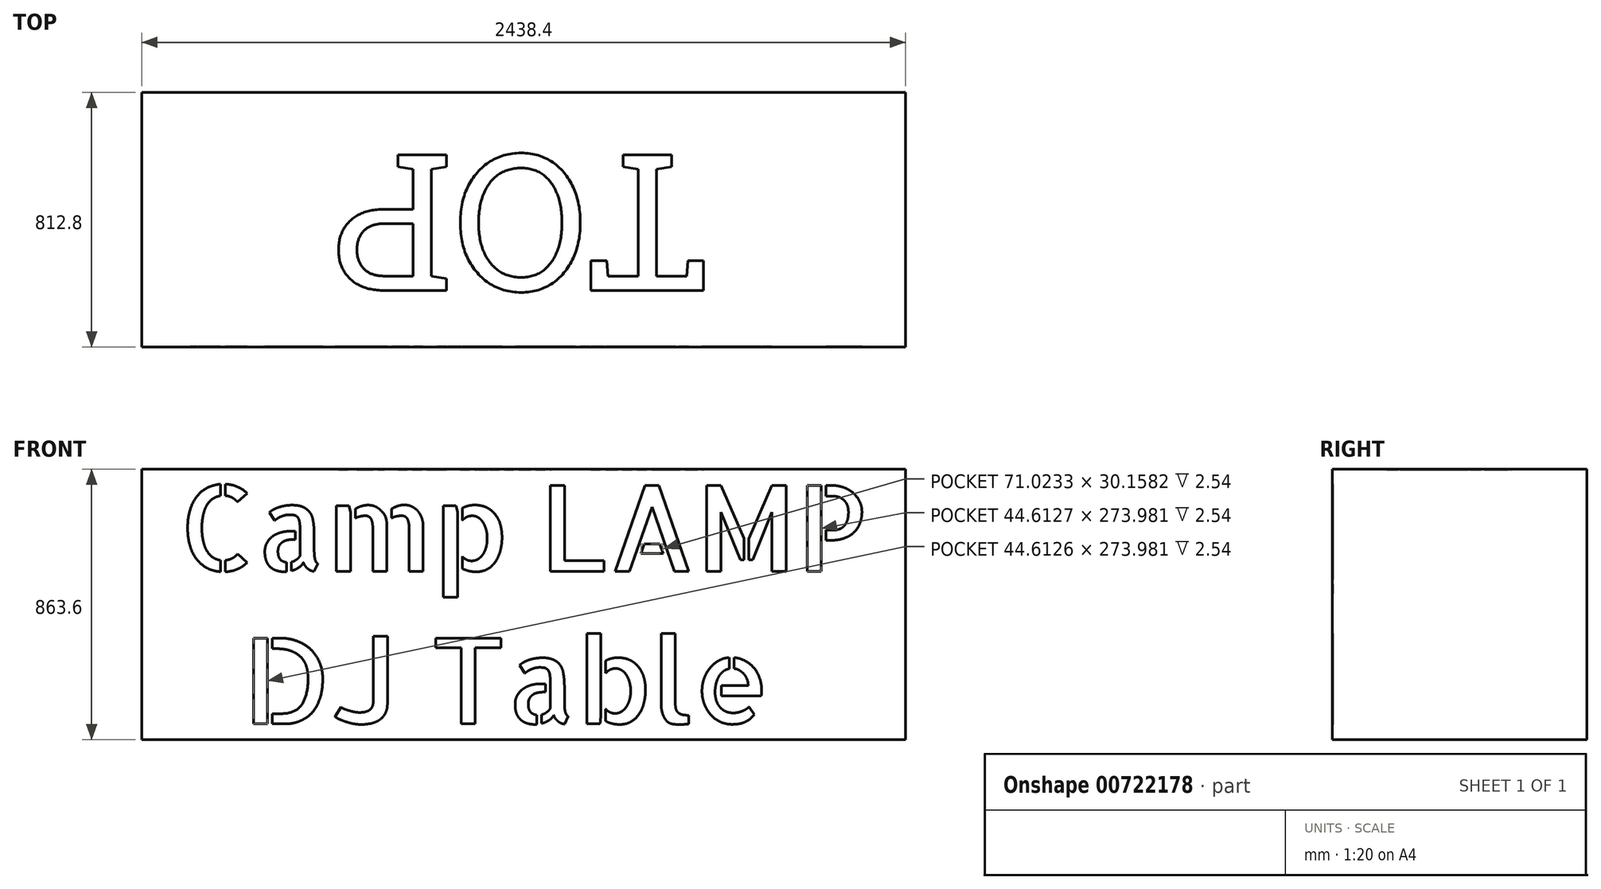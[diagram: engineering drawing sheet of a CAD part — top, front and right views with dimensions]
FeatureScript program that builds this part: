
annotation { "Feature Type Name" : "Feature", "Feature Type Description" : "" }
export const myFeature = defineFeature(function(context is Context, id is Id, definition is map)
    precondition{}
    {
        {
            var Q0;
            Q0=qCreatedBy(makeId("Front.planeOp"),FACE);
            var sketch = newSketch(context, id + "F0", { "sketchPlane" : qUnion([Q0])});
            skLineSegment(sketch, "E0.bottom", {"start": v(-1219.2, 0) * mm, "end": v(1219.2, 0) * mm});
            skLineSegment(sketch, "E0.top", {"start": v(-1219.2, 863.6) * mm, "end": v(1219.2, 863.6) * mm});
            skLineSegment(sketch, "E0.left", {"start": v(-1219.2, 0) * mm, "end": v(-1219.2, 863.6) * mm});
            skLineSegment(sketch, "E0.right", {"start": v(1219.2, 0) * mm, "end": v(1219.2, 863.6) * mm});
            skLineSegment(sketch, "E1", {"start": v(0, -157.9) * mm, "end": v(0, 863.6) * mm, "construction": true});
            skSolve(sketch);
        }
        {
            var Q0;
            Q0 = qSketchRegion(id + "F0", true);
            extrude(context, id + "F1", {"entities" : qUnion([Q0]), "oppositeDirection" : true, "depth" : 812.8 * mm, "offsetDistance" : 25.4 * mm});
        }
        {
            var Q0;
            Q0=makeQuery(id+"F1.opExtrude","CAP_FACE",FACE,{"disambiguationData":[OSD([sQuery(id+"F0.wireOp",EDGE,"E0.bottom"),sQuery(id+"F0.wireOp",EDGE,"E0.top"),sQuery(id+"F0.wireOp",EDGE,"E0.left"),sQuery(id+"F0.wireOp",EDGE,"E0.right")])],"isStart":true});
            var sketch = newSketch(context, id + "F2", { "sketchPlane" : qUnion([Q0])});
            skLineSegment(sketch, "E2", {"start": v(0, -126.3) * mm, "end": v(0, 537.73) * mm, "construction": true});
            skLineSegment(sketch, "E3", {"start": v(-1103.86, 537.73) * mm, "end": v(1103.86, 537.73) * mm, "construction": true});
            skText(sketch, "E4", { "text": "Camp LAMP\n  DJ Table", "fontName": "AllertaStencil-Regular.ttf"});
            const initialGuessF2  = {"E4": [-1.10202, 0.53773, 1, 0, 0.2741]};
            skSetInitialGuess(sketch, initialGuessF2);
            skSolve(sketch);
        }
        {
            var Q0;
            Q0 = qSketchRegion(id + "F2", true);
            extrude(context, id + "F3", {"entities" : qUnion([Q0]), "operationType" : NewBodyOperationType.REMOVE, "oppositeDirection" : true, "depth" : 2.54 * mm, "offsetDistance" : 25.4 * mm});
        }
        {
            var Q0;
            Q0=makeQuery(id+"F1.opExtrude","SWEPT_FACE",FACE,{"disambiguationData":[OSD([sQuery(id+"F0.wireOp",EDGE,"E0.top")])]});
            var sketch = newSketch(context, id + "F4", { "sketchPlane" : qUnion([Q0])});
            skText(sketch, "E5", { "text": "TOP", "fontName": "RobotoSlab-Regular.ttf"});
            const initialGuessF4  = {"E5": [0.58579, 0.61303, -1, 0, 0.43798]};
            skSetInitialGuess(sketch, initialGuessF4);
            skSolve(sketch);
        }
        {
            var Q0;
            Q0 = qSketchRegion(id + "F4", true);
            extrude(context, id + "F5", {"entities" : qUnion([Q0]), "operationType" : NewBodyOperationType.REMOVE, "oppositeDirection" : true, "depth" : 2.54 * mm, "offsetDistance" : 25.4 * mm});
        }
    });
